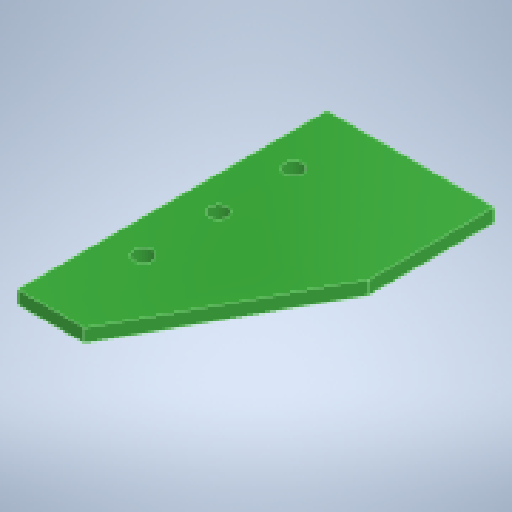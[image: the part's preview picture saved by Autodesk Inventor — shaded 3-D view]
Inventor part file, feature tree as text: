
AUTODESK INVENTOR PART (.ipt)
format: ipt  version: 2024.1 (Build 281209000, 209)  size: 243,200 bytes
history: native  units: in
note: dims shown in document units (in); Inventor stores cm internally (conversion verified against a paired STEP export)
features: extrude x2, sketch x2
ambient origin geometry x8: Origin, YZ Plane, XZ Plane, XY Plane, X Axis, Y Axis, Z Axis, Center Point
bodies: Solid1 (feature_tree)
feature tree (4):
  extrude  "Extrusion1"  Depth=1.4567in
  extrude  "Extrusion2"  Depth=0.063in
  sketch  "Sketch1"  dims[d0=1.4567in d1=0.315in]
  sketch  "Sketch2"  dims[d2=0.7874in d3=0.5906in d4=0.063in d5=0.0in d6=0.0866in d7=0.0866in d8=0.1575in d9=0.1575in d10=0.315in d11=0.3543in d12=0.0in d13=0.0in d14=0.0866in d15=0.1575in d16=0.3543in]
